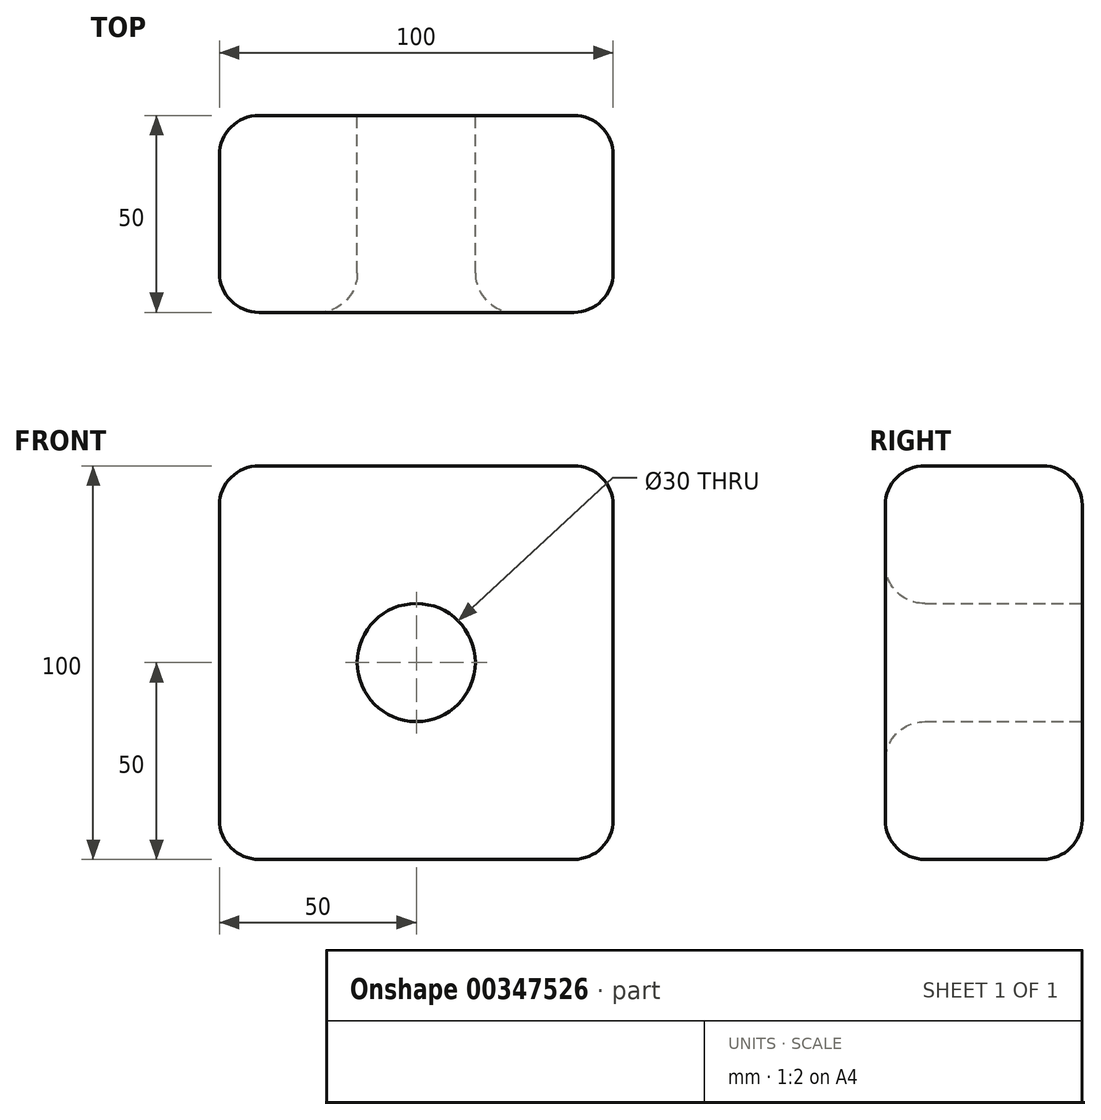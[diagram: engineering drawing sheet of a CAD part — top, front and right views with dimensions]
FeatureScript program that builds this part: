
annotation { "Feature Type Name" : "Feature", "Feature Type Description" : "" }
export const myFeature = defineFeature(function(context is Context, id is Id, definition is map)
    precondition{}
    {
        {
            var Q0;
            Q0=qCreatedBy(makeId("Front.planeOp"),FACE);
            var sketch = newSketch(context, id + "F0", { "sketchPlane" : qUnion([Q0])});
            skLineSegment(sketch, "E0.bottom", {"start": v(-50, 50) * mm, "end": v(50, 50) * mm});
            skLineSegment(sketch, "E0.top", {"start": v(-50, -50) * mm, "end": v(50, -50) * mm});
            skLineSegment(sketch, "E0.left", {"start": v(-50, 50) * mm, "end": v(-50, -50) * mm});
            skLineSegment(sketch, "E0.right", {"start": v(50, 50) * mm, "end": v(50, -50) * mm});
            skPoint(sketch, "E0.middle", {"position": v(0, 0) * mm});
            skCircle(sketch, "E1", {"center": v(0, 0) * mm, "radius": 15 * mm});
            skSolve(sketch);
        }
        {
            var Q0;
            Q0 = qSketchRegion(id + "F0", true);
            extrude(context, id + "F1", {"entities" : qUnion([Q0]), "endBound" : BoundingType.SYMMETRIC, "depth" : 100 * mm});
        }
        {
            var Q0;
            Q0=makeQuery(id+"F1.opExtrude","SWEPT_FACE",FACE,{"disambiguationData":[OSD([sQuery(id+"F0.wireOp",EDGE,"E0.right")])]});
            var Q1;
            Q1=makeQuery(id+"F1.opExtrude","CAP_FACE",FACE,{"disambiguationData":[OSD([sQuery(id+"F0.wireOp",EDGE,"E0.bottom"),sQuery(id+"F0.wireOp",EDGE,"E0.top"),sQuery(id+"F0.wireOp",EDGE,"E0.left"),sQuery(id+"F0.wireOp",EDGE,"E0.right")])],"isStart":false});
            var Q2;
            Q2=makeQuery(id+"F1.opExtrude","SWEPT_FACE",FACE,{"disambiguationData":[OSD([sQuery(id+"F0.wireOp",EDGE,"E0.bottom")])]});
            var Q3;
            Q3=makeQuery(id+"F1.opExtrude","CAP_EDGE",EDGE,{"disambiguationData":[OSD([sQuery(id+"F0.wireOp",EDGE,"E0.left")])],"isStart":true});
            var Q4;
            Q4=makeQuery(id+"F1.opExtrude","SWEPT_EDGE",EDGE,{"disambiguationData":[OSD([sQuery(id+"F0.wireOp",EDGE,"E0.top"),sQuery(id+"F0.wireOp",EDGE,"E0.left")])]});
            fillet(context, id + "F2", {"entities" : qUnion([Q0, Q1, Q2, Q3, Q4]), "radius" : 10 * mm, "tangentPropagation" : true, "allowEdgeOverflow" : false});
        }
        {
            var Q0;
            Q0 = qSketchRegion(id + "F0", true);
            extrude(context, id + "F3", {"entities" : qUnion([Q0]), "operationType" : NewBodyOperationType.REMOVE, "oppositeDirection" : true, "depth" : 50 * mm});
        }
        {
            var Q0;
            Q0=qCreatedBy(makeId("Top.planeOp"),FACE);
            var sketch = newSketch(context, id + "F4", { "sketchPlane" : qUnion([Q0])});
            skCircle(sketch, "E2", {"center": v(0, 0) * mm, "radius": 20 * mm});
            skSolve(sketch);
        }
        {
            var Q0;
            Q0=sQuery(id+"F4.wireOp",EDGE,"E2");
            extrude(context, id + "F5", {"bodyType" : ToolBodyType.SURFACE, "surfaceEntities" : qUnion([Q0]), "depth" : 50 * mm});
        }
        {
            var Q0;
            {var subQ0=sQuery(id+"F0.wireOp",EDGE,"E0.left");Q0=makeQuery(id+"F2.opFillet","BLEND_FACE",FACE,{"disambiguationData":[OSD([subQ0]),TDD([makeQuery(id+"F1.opExtrude","CAP_EDGE",EDGE,{"disambiguationData":[OSD([subQ0])],"isStart":true})])]});}
            var Q1;
            {var subQ0=sQuery(id+"F0.wireOp",EDGE,"E0.left");var subQ1=sQuery(id+"F0.wireOp",EDGE,"E0.top");Q1=makeQuery(id+"F2.opFillet","BLEND_FACE",FACE,{"disambiguationData":[OSD([subQ1,subQ0]),TDD([makeQuery(id+"F1.opExtrude","SWEPT_EDGE",EDGE,{"disambiguationData":[OSD([subQ1,subQ0])]})])]});}
            var Q2;
            {var subQ0=sQuery(id+"F0.wireOp",EDGE,"E0.left");var subQ1=sQuery(id+"F0.wireOp",EDGE,"E0.bottom");Q2=makeQuery(id+"F2.opFillet","BLEND_FACE",FACE,{"disambiguationData":[OSD([subQ1,subQ0]),TDD([makeQuery(id+"F1.opExtrude","CAP_VERTEX",VERTEX,{"disambiguationData":[OSD([subQ1,subQ0])],"isStart":true})])]});}
            var Q3;
            {var subQ0=sQuery(id+"F0.wireOp",EDGE,"E0.left");var subQ1=sQuery(id+"F0.wireOp",EDGE,"E0.bottom");Q3=makeQuery(id+"F2.opFillet","BLEND_FACE",FACE,{"disambiguationData":[OSD([subQ1,subQ0]),TDD([makeQuery(id+"F1.opExtrude","SWEPT_EDGE",EDGE,{"disambiguationData":[OSD([subQ1,subQ0])]})])]});}
            var Q4;
            {var subQ0=sQuery(id+"F0.wireOp",EDGE,"E0.left");var subQ1=sQuery(id+"F0.wireOp",EDGE,"E0.bottom");Q4=makeQuery(id+"F2.opFillet","BLEND_FACE",FACE,{"disambiguationData":[OSD([subQ1,subQ0]),TDD([makeQuery(id+"F1.opExtrude","CAP_VERTEX",VERTEX,{"disambiguationData":[OSD([subQ1,subQ0])],"isStart":false})])]});}
            var Q5;
            {var subQ0=sQuery(id+"F0.wireOp",EDGE,"E0.left");Q5=makeQuery(id+"F2.opFillet","BLEND_FACE",FACE,{"disambiguationData":[OSD([subQ0]),TDD([makeQuery(id+"F1.opExtrude","CAP_EDGE",EDGE,{"disambiguationData":[OSD([subQ0])],"isStart":false})])]});}
            var Q6;
            {var subQ0=sQuery(id+"F0.wireOp",EDGE,"E0.left");var subQ1=sQuery(id+"F0.wireOp",EDGE,"E0.top");Q6=makeQuery(id+"F2.opFillet","BLEND_FACE",FACE,{"disambiguationData":[OSD([subQ1,subQ0]),TDD([makeQuery(id+"F1.opExtrude","CAP_VERTEX",VERTEX,{"disambiguationData":[OSD([subQ1,subQ0])],"isStart":false})])]});}
            var Q7;
            Q7=makeQuery(id+"F1.opExtrude","SWEPT_FACE",FACE,{"disambiguationData":[OSD([sQuery(id+"F0.wireOp",EDGE,"E0.left")])]});
            var Q8;
            {var subQ0=sQuery(id+"F0.wireOp",EDGE,"E0.right");var subQ1=sQuery(id+"F0.wireOp",EDGE,"E0.top");Q8=makeQuery(id+"F2.opFillet","BLEND_FACE",FACE,{"disambiguationData":[OSD([subQ1,subQ0]),TDD([makeQuery(id+"F1.opExtrude","SWEPT_EDGE",EDGE,{"disambiguationData":[OSD([subQ1,subQ0])]})])]});}
            var Q9;
            {var subQ0=sQuery(id+"F0.wireOp",EDGE,"E0.right");Q9=makeQuery(id+"F2.opFillet","BLEND_FACE",FACE,{"disambiguationData":[OSD([subQ0]),TDD([makeQuery(id+"F1.opExtrude","CAP_EDGE",EDGE,{"disambiguationData":[OSD([subQ0])],"isStart":true})])]});}
            var Q10;
            {var subQ0=sQuery(id+"F0.wireOp",EDGE,"E0.right");Q10=makeQuery(id+"F2.opFillet","BLEND_EDGE",EDGE,{"blendedFrom":[makeQuery(id+"F1.opExtrude","CAP_EDGE",EDGE,{"disambiguationData":[OSD([subQ0])],"isStart":true}),makeQuery(id+"F1.opExtrude","SWEPT_FACE",FACE,{"disambiguationData":[OSD([subQ0])]})],"blendedInto":[makeQuery(id+"F1.opExtrude","SWEPT_FACE",FACE,{"disambiguationData":[OSD([subQ0])]})]});}
            var Q11;
            Q11=makeQuery(id+"F1.opExtrude","SWEPT_FACE",FACE,{"disambiguationData":[OSD([sQuery(id+"F0.wireOp",EDGE,"E0.right")])]});
            var Q12;
            {var subQ0=sQuery(id+"F0.wireOp",EDGE,"E0.top");Q12=makeQuery(id+"F2.opFillet","BLEND_EDGE",EDGE,{"blendedFrom":[makeQuery(id+"F1.opExtrude","CAP_VERTEX",VERTEX,{"disambiguationData":[OSD([subQ0,sQuery(id+"F0.wireOp",EDGE,"E0.right")])],"isStart":false}),makeQuery(id+"F1.opExtrude","CAP_EDGE",EDGE,{"disambiguationData":[OSD([subQ0])],"isStart":false})],"blendedInto":[]});}
            var Q13;
            Q13=makeQuery(id+"F1.opExtrude","CAP_FACE",FACE,{"disambiguationData":[OSD([sQuery(id+"F0.wireOp",EDGE,"E0.bottom"),sQuery(id+"F0.wireOp",EDGE,"E0.top"),sQuery(id+"F0.wireOp",EDGE,"E0.left"),sQuery(id+"F0.wireOp",EDGE,"E0.right")])],"isStart":false});
            var Q14;
            {var subQ0=sQuery(id+"F0.wireOp",EDGE,"E0.top");Q14=makeQuery(id+"F2.opFillet","BLEND_EDGE",EDGE,{"blendedFrom":[makeQuery(id+"F1.opExtrude","CAP_EDGE",EDGE,{"disambiguationData":[OSD([subQ0])],"isStart":false}),makeQuery(id+"F1.opExtrude","CAP_FACE",FACE,{"disambiguationData":[OSD([sQuery(id+"F0.wireOp",EDGE,"E0.bottom"),subQ0,sQuery(id+"F0.wireOp",EDGE,"E0.left"),sQuery(id+"F0.wireOp",EDGE,"E0.right")])],"isStart":false})],"blendedInto":[makeQuery(id+"F1.opExtrude","CAP_FACE",FACE,{"disambiguationData":[OSD([sQuery(id+"F0.wireOp",EDGE,"E0.bottom"),subQ0,sQuery(id+"F0.wireOp",EDGE,"E0.left"),sQuery(id+"F0.wireOp",EDGE,"E0.right")])],"isStart":false})]});}
            fillet(context, id + "F6", {"entities" : qUnion([Q0, Q1, Q2, Q3, Q4, Q5, Q6, Q7, Q8, Q9, Q10, Q11, Q12, Q13, Q14]), "radius" : 10 * mm, "tangentPropagation" : true, "allowEdgeOverflow" : false});
        }
    });
